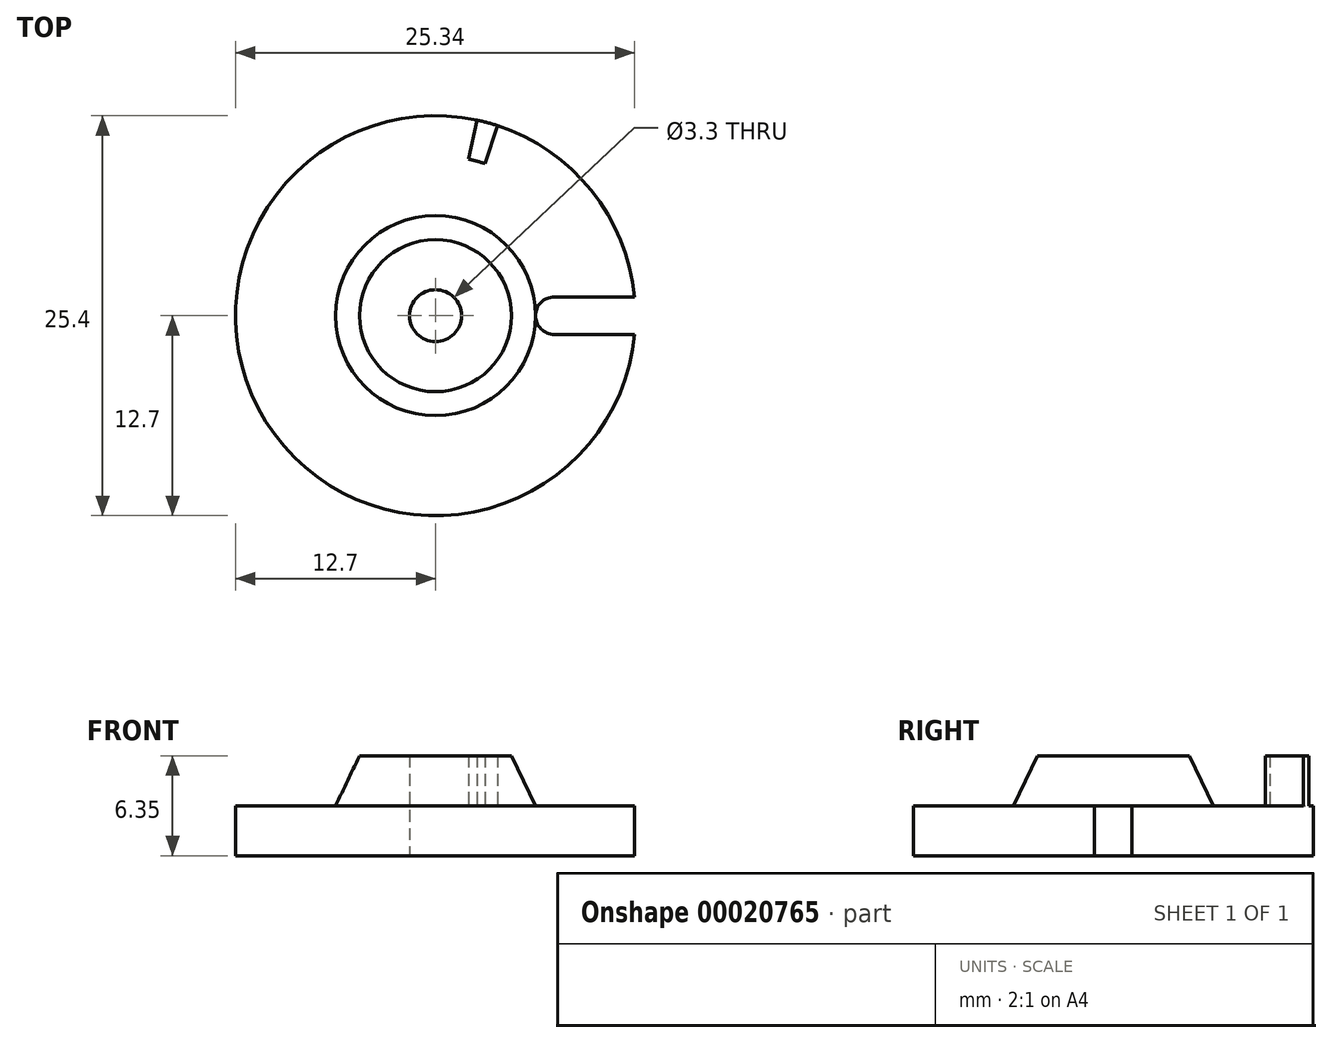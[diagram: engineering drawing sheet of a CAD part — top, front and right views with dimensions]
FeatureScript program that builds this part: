
annotation { "Feature Type Name" : "Feature", "Feature Type Description" : "" }
export const myFeature = defineFeature(function(context is Context, id is Id, definition is map)
    precondition{}
    {
        {
            var Q0;
            Q0=qCreatedBy(makeId("Front.planeOp"),FACE);
            var sketch = newSketch(context, id + "F0", { "sketchPlane" : qUnion([Q0])});
            skLineSegment(sketch, "E0", {"start": v(0, 0) * mm, "end": v(1.65, 0) * mm});
            skLineSegment(sketch, "E1", {"start": v(1.65, 0) * mm, "end": v(1.65, 6.35) * mm});
            skLineSegment(sketch, "E2", {"start": v(1.65, 0) * mm, "end": v(12.7, 0) * mm});
            skLineSegment(sketch, "E3", {"start": v(1.65, 6.35) * mm, "end": v(4.83, 6.35) * mm});
            skLineSegment(sketch, "E4", {"start": v(4.83, 6.35) * mm, "end": v(6.35, 3.18) * mm});
            skLineSegment(sketch, "E5", {"start": v(6.35, 3.18) * mm, "end": v(12.7, 3.18) * mm});
            skLineSegment(sketch, "E6", {"start": v(12.7, 3.18) * mm, "end": v(12.7, 0) * mm});
            skLineSegment(sketch, "E7", {"start": v(0, 0) * mm, "end": v(0, 3.83) * mm});
            skSolve(sketch);
        }
        {
            var Q0;
            Q0=makeQuery(id+"F0.imprint","IMPRINT",FACE,{"disambiguationData":[TD([[makeQuery(id+"F0.imprint","IMPRINT",EDGE,{"derivedFrom":sQuery(id+"F0.wireOp",EDGE,"E1")}),-1.0]])]});
            var Q1;
            Q1=sQuery(id+"F0.wireOp",EDGE,"E7");
            revolve(context, id + "F1", {"entities" : qUnion([Q0]), "axis" : qUnion([Q1]), "revolveType" : RevolveType.FULL});
        }
        {
            var Q0;
            Q0=makeQuery(id+"F1.opRevolve","SWEPT_FACE",FACE,{"disambiguationData":[OSD([sQuery(id+"F0.wireOp",EDGE,"E2")])]});
            var sketch = newSketch(context, id + "F2", { "sketchPlane" : qUnion([Q0])});
            skLineSegment(sketch, "E8", {"start": v(6.35, 0) * mm, "end": v(0, 0) * mm});
            skArc(sketch, "E9", {"start": v(7.54, 1.2) * mm, "mid": v(6.35, 0) * mm, "end": v(7.54, -1.2) * mm});
            skLineSegment(sketch, "E10", {"start": v(7.54, 1.2) * mm, "end": v(12.64, 1.2) * mm});
            skLineSegment(sketch, "E11", {"start": v(7.54, -1.2) * mm, "end": v(12.64, -1.2) * mm});
            skCircle(sketch, "E12.0", {"center": v(0, 0) * mm, "radius": 12.7 * mm});
            skSolve(sketch);
        }
        {
            var Q0;
            {var subQ2=sQuery(id+"F2.wireOp",EDGE,"E10");Q0=makeQuery(id+"F2.imprint","IMPRINT",FACE,{"disambiguationData":[TD([[makeQuery(id+"F2.imprint","IMPRINT",EDGE,{"derivedFrom":subQ2}),-1.0]])]});}
            extrude(context, id + "F3", {"entities" : qUnion([Q0]), "operationType" : NewBodyOperationType.REMOVE, "endBound" : BoundingType.THROUGH_ALL, "oppositeDirection" : true, "depth" : 25.4 * mm});
        }
        {
            var Q0;
            Q0=makeQuery(id+"F1.opRevolve","SWEPT_FACE",FACE,{"disambiguationData":[OSD([sQuery(id+"F0.wireOp",EDGE,"E2")])]});
            var sketch = newSketch(context, id + "F4", { "sketchPlane" : qUnion([Q0])});
            skLineSegment(sketch, "E13", {"start": v(0, 0) * mm, "end": v(3.92, -12.08) * mm});
            skLineSegment(sketch, "E14", {"start": v(0, 0) * mm, "end": v(2.64, -12.42) * mm});
            skArc(sketch, "E15", {"start": v(2.11, -9.94) * mm, "mid": v(2.63, -9.81) * mm, "end": v(3.14, -9.66) * mm});
            skSolve(sketch);
        }
        {
            var Q0;
            {var subQ0=sQuery(id+"F4.wireOp",EDGE,"E15");Q0=makeQuery(id+"F4.imprint","IMPRINT",FACE,{"disambiguationData":[TD([[makeQuery(id+"F4.imprint","IMPRINT",EDGE,{"derivedFrom":subQ0}),-1.0]])]});}
            extrude(context, id + "F5", {"entities" : qUnion([Q0]), "operationType" : NewBodyOperationType.ADD, "oppositeDirection" : true, "depth" : 6.35 * mm});
        }
    });
